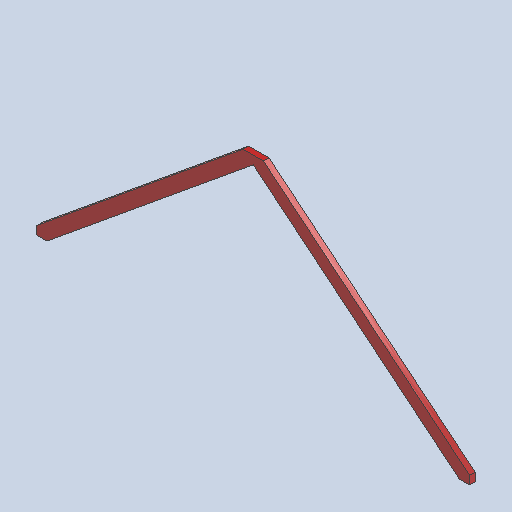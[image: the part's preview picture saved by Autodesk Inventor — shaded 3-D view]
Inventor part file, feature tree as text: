
AUTODESK INVENTOR PART (.ipt)
format: ipt  version: 2025 (Build 290162000, 162)  size: 267,776 bytes
history: native  units: in
note: dims shown in document units (in); Inventor stores cm internally (conversion verified against a paired STEP export)
features: other x7, reference x4, extrude x1, sketch x1
ambient origin geometry x8: Origin, YZ Plane, XZ Plane, XY Plane, X Axis, Y Axis, Z Axis, Center Point
bodies: Solid1 (feature_tree)
feature tree (13):
  extrude  "Extrusion1"  [1 undecoded]
  sketch  "Sketch1"  dims[d4=1.5in d5=0.0in]
  reference  "Reference1"
  reference  "Reference2"
  reference  "Reference3"
  reference  "Reference4"
  other  "<userpath>\Documents\USCTigerBurn24\Tburn24\F_Legs1\B_Legs0.iam"
  other  "B_Legs0.iam"
  other  "8'x2x4:2"
  other  "4x2x4:2"
  other  "8'x2x4:4"
  other  "4x2x4:3"
  other  "Finish1"
note: 1 required parameter value undecoded (feature->parameter linkage not recoverable at this tier; creation-order binding heuristic only, values carry confidence <= 0.55)
